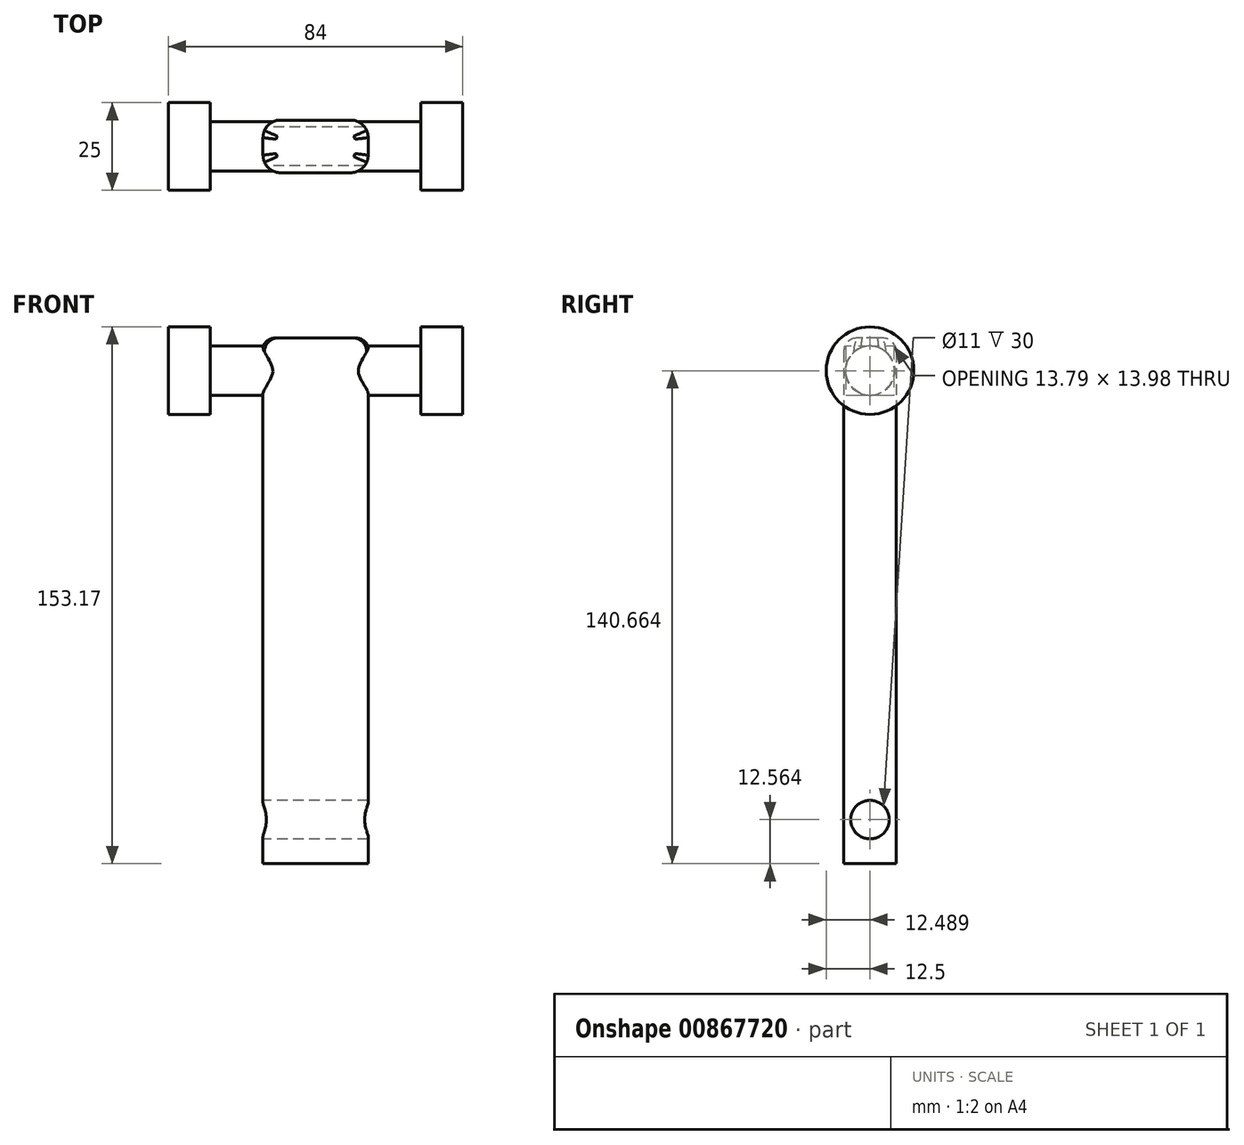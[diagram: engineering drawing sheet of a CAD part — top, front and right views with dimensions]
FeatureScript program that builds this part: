
annotation { "Feature Type Name" : "Feature", "Feature Type Description" : "" }
export const myFeature = defineFeature(function(context is Context, id is Id, definition is map)
    precondition{}
    {
        {
            var Q0;
            Q0=qCreatedBy(makeId("Top.planeOp"),FACE);
            var sketch = newSketch(context, id + "F0", { "sketchPlane" : qUnion([Q0])});
            skLineSegment(sketch, "E0.bottom", {"start": v(15, -7.5) * mm, "end": v(-15, -7.5) * mm});
            skLineSegment(sketch, "E0.top", {"start": v(15, 7.5) * mm, "end": v(-15, 7.5) * mm});
            skLineSegment(sketch, "E0.left", {"start": v(15, -7.5) * mm, "end": v(15, 7.5) * mm});
            skLineSegment(sketch, "E0.right", {"start": v(-15, -7.5) * mm, "end": v(-15, 7.5) * mm});
            skSolve(sketch);
        }
        {
            var Q0;
            Q0=makeQuery(id+"F0.imprint","IMPRINT",FACE,{"disambiguationData":[TD([[makeQuery(id+"F0.imprint","IMPRINT",EDGE,{"derivedFrom":sQuery(id+"F0.wireOp",EDGE,"E0.bottom")}),-1.0]])]});
            extrude(context, id + "F1", {"entities" : qUnion([Q0]), "depth" : 150 * mm, "offsetDistance" : 25 * mm});
        }
        {
            var Q0;
            Q0=makeQuery(id+"F1.opExtrude","SWEPT_FACE",FACE,{"disambiguationData":[OSD([sQuery(id+"F0.wireOp",EDGE,"E0.right")])]});
            var sketch = newSketch(context, id + "F2", { "sketchPlane" : qUnion([Q0])});
            skCircle(sketch, "E1", {"center": v(0, 12.56) * mm, "radius": 5.5 * mm});
            skSolve(sketch);
        }
        {
            var Q0;
            Q0=makeQuery(id+"F2.imprint","IMPRINT",FACE,{"disambiguationData":[TD([[makeQuery(id+"F2.imprint","IMPRINT",EDGE,{"derivedFrom":sQuery(id+"F2.wireOp",EDGE,"E1")}),1.0]])]});
            extrude(context, id + "F3", {"entities" : qUnion([Q0]), "operationType" : NewBodyOperationType.REMOVE, "oppositeDirection" : true, "depth" : 30 * mm, "offsetDistance" : 25 * mm, "hasSecondDirection" : true, "secondDirectionOppositeDirection" : false, "secondDirectionDepth" : 30 * mm});
        }
        {
            var Q0;
            Q0=makeQuery(id+"F1.opExtrude","SWEPT_EDGE",EDGE,{"disambiguationData":[OSD([sQuery(id+"F0.wireOp",EDGE,"E0.top"),sQuery(id+"F0.wireOp",EDGE,"E0.right")])]});
            var Q1;
            Q1=makeQuery(id+"F1.opExtrude","SWEPT_EDGE",EDGE,{"disambiguationData":[OSD([sQuery(id+"F0.wireOp",EDGE,"E0.bottom"),sQuery(id+"F0.wireOp",EDGE,"E0.right")])]});
            var Q2;
            Q2=makeQuery(id+"F1.opExtrude","SWEPT_EDGE",EDGE,{"disambiguationData":[OSD([sQuery(id+"F0.wireOp",EDGE,"E0.bottom"),sQuery(id+"F0.wireOp",EDGE,"E0.left")])]});
            var Q3;
            Q3=makeQuery(id+"F1.opExtrude","SWEPT_EDGE",EDGE,{"disambiguationData":[OSD([sQuery(id+"F0.wireOp",EDGE,"E0.top"),sQuery(id+"F0.wireOp",EDGE,"E0.left")])]});
            fillet(context, id + "F4", {"entities" : qUnion([Q0, Q1, Q2, Q3]), "radius" : 5 * mm, "tangentPropagation" : true, "allowEdgeOverflow" : false});
        }
        {
            var Q0;
            Q0=qCreatedBy(makeId("Right.planeOp"),FACE);
            var sketch = newSketch(context, id + "F5", { "sketchPlane" : qUnion([Q0])});
            skCircle(sketch, "E2", {"center": v(0, 140.67) * mm, "radius": 7 * mm});
            skSolve(sketch);
        }
        {
            var Q0;
            Q0 = qSketchRegion(id + "F5", true);
            extrude(context, id + "F6", {"entities" : qUnion([Q0]), "operationType" : NewBodyOperationType.ADD, "depth" : 30 * mm, "offsetDistance" : 25 * mm, "hasSecondDirection" : true, "secondDirectionOppositeDirection" : true, "secondDirectionDepth" : 30 * mm});
        }
        {
            var Q0;
            Q0=makeQuery(id+"F6.opExtrude","CAP_FACE",FACE,{"disambiguationData":[OSD([sQuery(id+"F5.wireOp",EDGE,"E2")])],"isStart":false});
            var sketch = newSketch(context, id + "F7", { "sketchPlane" : qUnion([Q0])});
            skCircle(sketch, "E3", {"center": v(0, 140.67) * mm, "radius": 12.5 * mm});
            skSolve(sketch);
        }
        {
            var Q0;
            Q0 = qSketchRegion(id + "F7", true);
            extrude(context, id + "F8", {"entities" : qUnion([Q0]), "operationType" : NewBodyOperationType.ADD, "depth" : 12 * mm, "offsetDistance" : 25 * mm});
        }
        {
            var Q0;
            Q0=makeQuery(id+"F6.opExtrude","CAP_FACE",FACE,{"disambiguationData":[OSD([sQuery(id+"F5.wireOp",EDGE,"E2")])],"isStart":true});
            var sketch = newSketch(context, id + "F9", { "sketchPlane" : qUnion([Q0])});
            skCircle(sketch, "E4", {"center": v(0, 140.67) * mm, "radius": 12.5 * mm});
            skSolve(sketch);
        }
        {
            var Q0;
            Q0 = qSketchRegion(id + "F9", true);
            extrude(context, id + "F10", {"entities" : qUnion([Q0]), "operationType" : NewBodyOperationType.ADD, "depth" : 12 * mm, "offsetDistance" : 25 * mm});
        }
        {
            var Q0;
            Q0=makeQuery(id+"F1.opExtrude","CAP_FACE",FACE,{"disambiguationData":[OSD([sQuery(id+"F0.wireOp",EDGE,"E0.bottom"),sQuery(id+"F0.wireOp",EDGE,"E0.top"),sQuery(id+"F0.wireOp",EDGE,"E0.left"),sQuery(id+"F0.wireOp",EDGE,"E0.right")])],"isStart":false});
            fillet(context, id + "F11", {"entities" : qUnion([Q0]), "radius" : 4 * mm, "tangentPropagation" : true, "allowEdgeOverflow" : false});
        }
    });
